# Revit family: xxxPet_Fountain-Murdock_Mfg-GUT_Series.rfa
name_source: partatom
category: Plumbing Fixtures
units: mm (PartAtom-declared; Revit-internal decimal feet)

## family parameters
Cut with Voids When Loaded = Yes
Host = Face
OmniClass Number = 23.65.70.14.11
OmniClass Title = Drinking Fountains/Coolers
Part Type = Normal
Room Calculation Point = No
Round Connector Dimension = Use Diameter
Shared = Yes

## types (2) — shared parameters
-FRU1 Underground freeze resistant valve = No
-RFS Round free standing bowl = No
Activation = Self-Closing Button
Assembly Code = D2010820
CW Connection = Yes
CWFU = 1.5
Cold Water Connection Diameter = 1/2"
Default Elevation = 0"
Description = Round Concrete Pet Fountain
Finish- Bowl = Stainless Steel-Murdock-Type 304-Grey
Finish- Bubbler = Stainless Steel-Murdock-Polished
HW Connection = No
Height = 9"
IAPMO Compliance = NSF/ANSI  61,  Section 9,  Public  Law  111-380(NO-LEAD), and CHSC 116875
Installation Instruction Link = https://www.murdockmfg.com
Installation Type = Wall Mounted
Length = 12 1/2"
Manufacturer = Murdock Manufacturing
Min Max. Operating Pressure = 30 to 100 psi
Price = Prices may vary. Please consult Manufacturer Representative for most up-to-date price list.
Product Documentation Link = https://www.murdockmfg.com
Product Page URL = https://www.murdockmfg.com
URL = https://www.murdockmfg.com
Vent Connection = No
WFU = 2
Warranty Documentation Link = https://www.murdockmfg.com
Waste Connection = Yes
Waste Connection Diameter = 1 1/4"
Water Pressure = 20-105  psig
Width = 13"
cUPC Compliant = Yes
rfs BD = 3/8"
rfs gap = 5"
zero-valued in all types: HWFU

## per-type parameters (varying)
| type | Finish | Material |
| GUT18-PF | Aggregate-Murdock-Tan | Aggregate-Murdock-Tan |
| GUT19-PF | Aggregate-Murdock-Brown | Aggregate-Murdock-Brown |

note: column(s) folded — value = type name in every type: Model

## geometry (parser evidence)
native form markers: Sweep x2
no freeform markers — native parametric forms only
